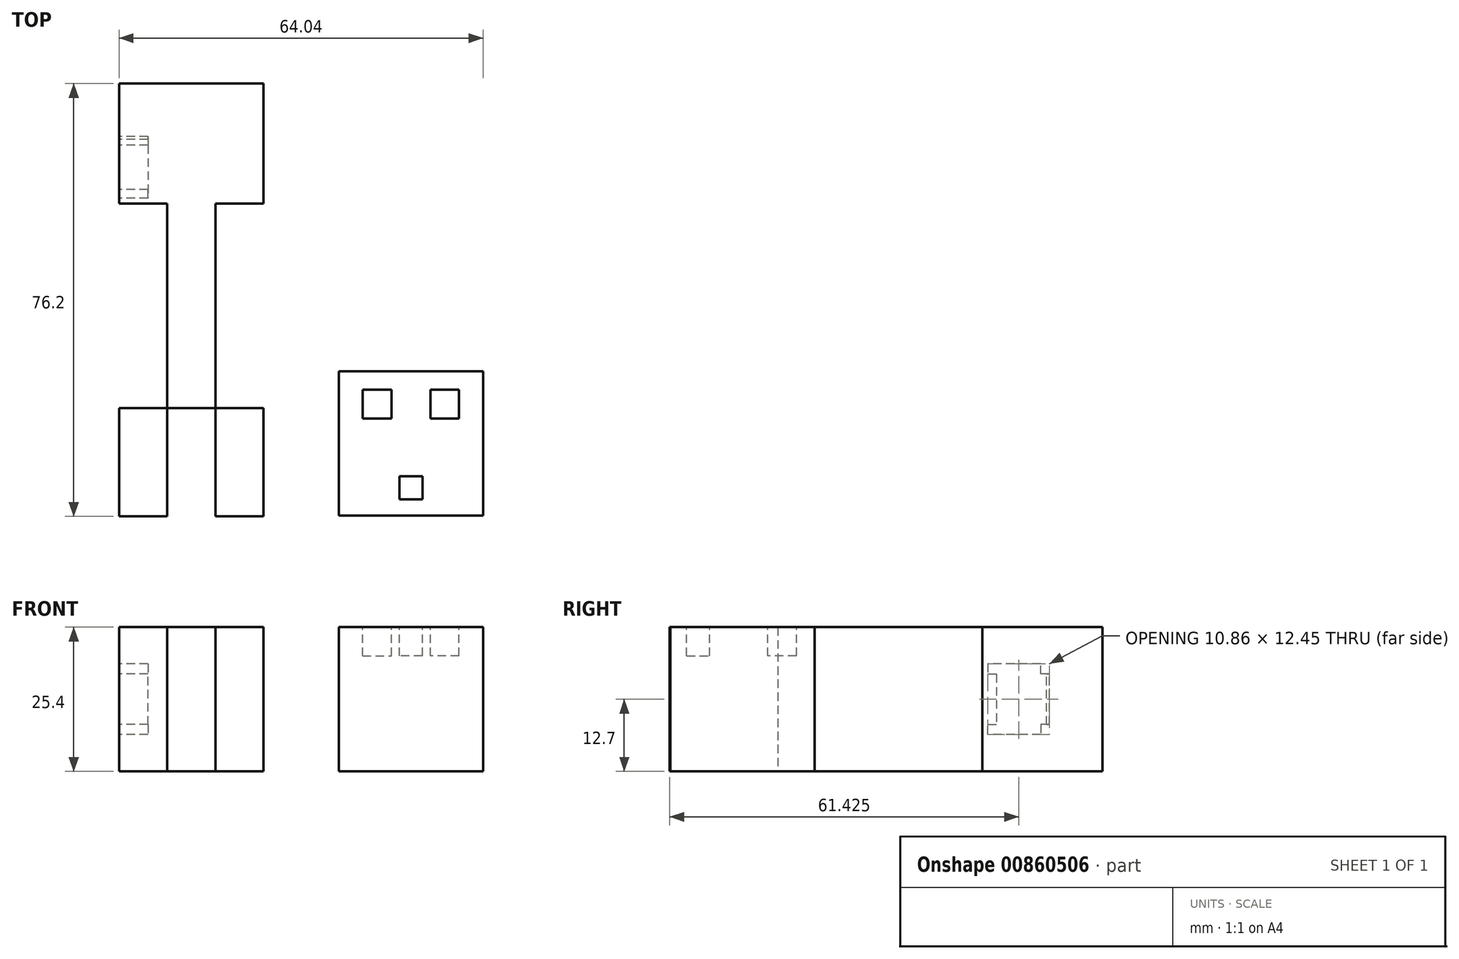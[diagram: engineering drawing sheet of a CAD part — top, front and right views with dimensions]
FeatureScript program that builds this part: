
annotation { "Feature Type Name" : "Feature", "Feature Type Description" : "" }
export const myFeature = defineFeature(function(context is Context, id is Id, definition is map)
    precondition{}
    {
        {
            var Q0;
            Q0=qCreatedBy(makeId("Top.planeOp"),FACE);
            var sketch = newSketch(context, id + "F0", { "sketchPlane" : qUnion([Q0])});
            skLineSegment(sketch, "E0.bottom", {"start": v(12.7, -12.7) * mm, "end": v(-12.7, -12.7) * mm});
            skLineSegment(sketch, "E0.top", {"start": v(12.7, 12.7) * mm, "end": v(-12.7, 12.7) * mm});
            skLineSegment(sketch, "E0.left", {"start": v(12.7, -12.7) * mm, "end": v(12.7, 12.7) * mm});
            skLineSegment(sketch, "E0.right", {"start": v(-12.7, -12.7) * mm, "end": v(-12.7, 12.7) * mm});
            skPoint(sketch, "E0.middle", {"position": v(0, 0) * mm});
            skSolve(sketch);
        }
        {
            var Q0;
            Q0 = qSketchRegion(id + "F0", true);
            extrude(context, id + "F1", {"entities" : qUnion([Q0]), "depth" : 25.4 * mm, "offsetDistance" : 25.4 * mm});
        }
        {
            var Q0;
            Q0=makeQuery(id+"F1.opExtrude","CAP_FACE",FACE,{"disambiguationData":[OSD([sQuery(id+"F0.wireOp",EDGE,"E0.bottom"),sQuery(id+"F0.wireOp",EDGE,"E0.top"),sQuery(id+"F0.wireOp",EDGE,"E0.left"),sQuery(id+"F0.wireOp",EDGE,"E0.right")])],"isStart":false});
            var sketch = newSketch(context, id + "F2", { "sketchPlane" : qUnion([Q0])});
            skLineSegment(sketch, "E1.bottom", {"start": v(2.03, -9.85) * mm, "end": v(-2.03, -9.85) * mm});
            skLineSegment(sketch, "E1.top", {"start": v(2.03, -5.8) * mm, "end": v(-2.03, -5.8) * mm});
            skLineSegment(sketch, "E1.left", {"start": v(2.03, -9.85) * mm, "end": v(2.03, -5.8) * mm});
            skLineSegment(sketch, "E1.right", {"start": v(-2.03, -9.85) * mm, "end": v(-2.03, -5.8) * mm});
            skPoint(sketch, "E1.middle", {"position": v(0, -7.82) * mm});
            skPoint(sketch, "E1.middle.positionSnap0", {"position": v(0, -12.7) * mm});
            skPoint(sketch, "E1.centerSnap0", {"position": v(0, -12.7) * mm});
            skLineSegment(sketch, "E2.bottom", {"start": v(-8.51, 9.47) * mm, "end": v(-3.43, 9.47) * mm});
            skLineSegment(sketch, "E2.top", {"start": v(-8.51, 4.4) * mm, "end": v(-3.43, 4.4) * mm});
            skLineSegment(sketch, "E2.left", {"start": v(-8.51, 9.47) * mm, "end": v(-8.51, 4.4) * mm});
            skLineSegment(sketch, "E2.right", {"start": v(-3.43, 9.47) * mm, "end": v(-3.43, 4.4) * mm});
            skLineSegment(sketch, "E3", {"start": v(12.7, 12.7) * mm, "end": v(12.7, 9.47) * mm});
            skLineSegment(sketch, "E4", {"start": v(12.7, 9.47) * mm, "end": v(8.5, 9.47) * mm});
            skLineSegment(sketch, "E5.bottom", {"start": v(8.5, 9.47) * mm, "end": v(3.43, 9.47) * mm});
            skLineSegment(sketch, "E5.top", {"start": v(8.5, 4.4) * mm, "end": v(3.43, 4.4) * mm});
            skLineSegment(sketch, "E5.left", {"start": v(8.5, 9.47) * mm, "end": v(8.5, 4.4) * mm});
            skLineSegment(sketch, "E5.right", {"start": v(3.43, 9.47) * mm, "end": v(3.43, 4.4) * mm});
            skSolve(sketch);
        }
        {
            var Q0;
            Q0 = qSketchRegion(id + "F2", true);
            extrude(context, id + "F3", {"entities" : qUnion([Q0]), "operationType" : NewBodyOperationType.REMOVE, "oppositeDirection" : true, "depth" : 5.08 * mm, "offsetDistance" : 25.4 * mm});
        }
        {
            var Q0;
            Q0=qCreatedBy(makeId("Top.planeOp"),FACE);
            var sketch = newSketch(context, id + "F4", { "sketchPlane" : qUnion([Q0])});
            skLineSegment(sketch, "E6.bottom", {"start": v(-51.34, 63.37) * mm, "end": v(-25.94, 63.37) * mm});
            skLineSegment(sketch, "E6.top", {"start": v(-51.34, -12.83) * mm, "end": v(-42.87, -12.83) * mm});
            skLineSegment(sketch, "E6.left", {"start": v(-51.34, 63.37) * mm, "end": v(-51.34, 42.22) * mm});
            skLineSegment(sketch, "E6.right", {"start": v(-25.94, 63.37) * mm, "end": v(-25.94, 42.22) * mm});
            skLineSegment(sketch, "E7", {"start": v(-51.34, 6.22) * mm, "end": v(-51.34, -12.83) * mm});
            skLineSegment(sketch, "E8", {"start": v(-51.34, -12.83) * mm, "end": v(-51.34, 6.22) * mm});
            skLineSegment(sketch, "E9", {"start": v(-51.34, 42.22) * mm, "end": v(-51.34, 44.32) * mm});
            skPoint(sketch, "E10", {"position": v(-51.34, 42.22) * mm});
            skLineSegment(sketch, "E11", {"start": v(-51.34, 42.22) * mm, "end": v(-25.94, 42.22) * mm});
            skLineSegment(sketch, "E12", {"start": v(-51.34, 6.22) * mm, "end": v(-25.94, 6.22) * mm});
            skLineSegment(sketch, "E13", {"start": v(-51.34, 42.22) * mm, "end": v(-42.87, 42.22) * mm});
            skLineSegment(sketch, "E14", {"start": v(-42.87, 42.22) * mm, "end": v(-34.4, 42.22) * mm});
            skLineSegment(sketch, "E15", {"start": v(-34.4, 42.22) * mm, "end": v(-25.94, 42.22) * mm});
            skLineSegment(sketch, "E16", {"start": v(-42.87, 42.22) * mm, "end": v(-42.87, 6.22) * mm});
            skLineSegment(sketch, "E17", {"start": v(-42.87, 6.22) * mm, "end": v(-38.64, 6.22) * mm});
            skLineSegment(sketch, "E18", {"start": v(-38.64, 6.22) * mm, "end": v(-34.4, 6.22) * mm});
            skLineSegment(sketch, "E19", {"start": v(-34.4, 6.22) * mm, "end": v(-34.4, 42.22) * mm});
            skPoint(sketch, "E20.orphan", {"position": v(-51.34, 25.27) * mm});
            skLineSegment(sketch, "E21.trimOffspring", {"start": v(-25.94, 6.22) * mm, "end": v(-25.94, -12.83) * mm});
            skLineSegment(sketch, "E22", {"start": v(-34.4, 6.22) * mm, "end": v(-34.4, -12.83) * mm});
            skLineSegment(sketch, "E23", {"start": v(-42.87, 6.22) * mm, "end": v(-42.87, -12.83) * mm});
            skLineSegment(sketch, "E24.trimOffspring", {"start": v(-34.4, -12.83) * mm, "end": v(-25.94, -12.83) * mm});
            skSolve(sketch);
        }
        {
            var Q0;
            Q0 = qSketchRegion(id + "F4", true);
            extrude(context, id + "F5", {"entities" : qUnion([Q0]), "depth" : 25.4 * mm, "offsetDistance" : 25.4 * mm});
        }
        {
            var Q0;
            Q0 = qSketchRegion(id + "F4", true);
            extrude(context, id + "F6", {"entities" : qUnion([Q0]), "depth" : 25.4 * mm, "offsetDistance" : 25.4 * mm});
        }
        {
            var Q0;
            Q0=makeQuery(id+"F5.opExtrude","SWEPT_FACE",FACE,{"disambiguationData":[OSD([sQuery(id+"F4.wireOp",EDGE,"E6.left"),sQuery(id+"F4.wireOp",EDGE,"E9")])]});
            var sketch = newSketch(context, id + "F7", { "sketchPlane" : qUnion([Q0])});
            skLineSegment(sketch, "E25", {"start": v(-63.37, 0) * mm, "end": v(-58.85, 0) * mm});
            skLineSegment(sketch, "E26", {"start": v(-58.85, 0) * mm, "end": v(-58.85, 3.43) * mm});
            skLineSegment(sketch, "E27.bottom", {"start": v(-58.85, 3.43) * mm, "end": v(-54.02, 3.43) * mm});
            skLineSegment(sketch, "E27.top", {"start": v(-58.85, 8.26) * mm, "end": v(-54.02, 8.26) * mm});
            skLineSegment(sketch, "E27.left", {"start": v(-58.85, 3.43) * mm, "end": v(-58.85, 8.26) * mm});
            skLineSegment(sketch, "E27.right", {"start": v(-54.02, 3.43) * mm, "end": v(-54.02, 8.26) * mm});
            skLineSegment(sketch, "E28", {"start": v(-63.37, 25.4) * mm, "end": v(-58.85, 25.4) * mm});
            skLineSegment(sketch, "E29", {"start": v(-58.85, 25.4) * mm, "end": v(-58.85, 21.97) * mm});
            skLineSegment(sketch, "E30.bottom", {"start": v(-58.85, 21.97) * mm, "end": v(-54.02, 21.97) * mm});
            skLineSegment(sketch, "E30.top", {"start": v(-58.85, 17.14) * mm, "end": v(-54.02, 17.14) * mm});
            skLineSegment(sketch, "E30.left", {"start": v(-58.85, 21.97) * mm, "end": v(-58.85, 17.14) * mm});
            skLineSegment(sketch, "E30.right", {"start": v(-54.02, 21.97) * mm, "end": v(-54.02, 17.14) * mm});
            skLineSegment(sketch, "E31", {"start": v(-54.02, 8.26) * mm, "end": v(-52.5, 8.26) * mm});
            skLineSegment(sketch, "E32", {"start": v(-52.5, 8.26) * mm, "end": v(-52.5, 6.48) * mm});
            skLineSegment(sketch, "E33", {"start": v(-52.5, 6.48) * mm, "end": v(-43.17, 6.48) * mm});
            skLineSegment(sketch, "E34", {"start": v(-43.17, 6.48) * mm, "end": v(-43.17, 8.26) * mm});
            skLineSegment(sketch, "E35", {"start": v(-43.17, 8.26) * mm, "end": v(-44.7, 8.26) * mm});
            skLineSegment(sketch, "E36", {"start": v(-54.02, 17.14) * mm, "end": v(-52.5, 17.14) * mm});
            skLineSegment(sketch, "E37", {"start": v(-52.5, 17.14) * mm, "end": v(-52.5, 18.92) * mm});
            skLineSegment(sketch, "E38", {"start": v(-52.5, 18.92) * mm, "end": v(-43.17, 18.92) * mm});
            skLineSegment(sketch, "E39", {"start": v(-43.17, 18.92) * mm, "end": v(-43.17, 17.14) * mm});
            skLineSegment(sketch, "E40", {"start": v(-43.17, 17.14) * mm, "end": v(-44.7, 17.14) * mm});
            skLineSegment(sketch, "E41", {"start": v(-44.7, 17.14) * mm, "end": v(-44.7, 8.26) * mm});
            skLineSegment(sketch, "E42", {"start": v(-54.02, 8.26) * mm, "end": v(-54.02, 17.14) * mm});
            skSolve(sketch);
        }
        {
            var Q0;
            Q0=makeQuery(id+"F7.imprint","IMPRINT",FACE,{"disambiguationData":[TD([[makeQuery(id+"F7.imprint","IMPRINT",EDGE,{"derivedFrom":sQuery(id+"F7.wireOp",EDGE,"E31")}),1.0]])]});
            extrude(context, id + "F8", {"entities" : qUnion([Q0]), "operationType" : NewBodyOperationType.REMOVE, "oppositeDirection" : true, "depth" : 5.08 * mm, "offsetDistance" : 25.4 * mm});
        }
        {
            var Q0;
            {var subQ1=sQuery(id+"F7.wireOp",EDGE,"E42");Q0=makeQuery(id+"F8.boolean.opBoolean","COPY",FACE,{"disambiguationData":[TD([makeQuery(id+"F5.opExtrude","SWEPT_FACE",FACE,{"disambiguationData":[OSD([sQuery(id+"F4.wireOp",EDGE,"E6.left"),sQuery(id+"F4.wireOp",EDGE,"E9")])]})])],"derivedFrom":makeQuery(id+"F8.opExtrude","SWEPT_FACE",FACE,{"disambiguationData":[OSD([subQ1])]})});}
            extrude(context, id + "F9", {"entities" : qUnion([Q0]), "depth" : 0.5 * mm, "offsetDistance" : 25.4 * mm});
        }
    });
